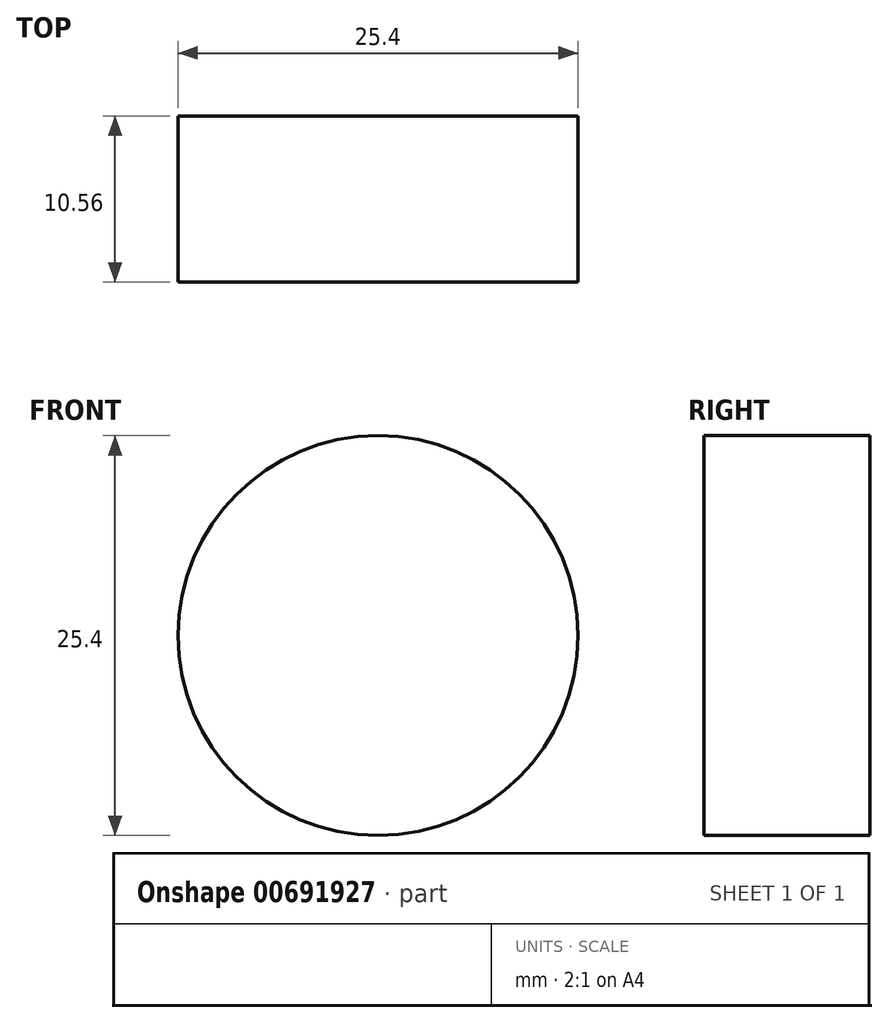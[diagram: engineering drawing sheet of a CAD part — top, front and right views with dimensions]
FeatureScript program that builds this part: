
annotation { "Feature Type Name" : "Feature", "Feature Type Description" : "" }
export const myFeature = defineFeature(function(context is Context, id is Id, definition is map)
    precondition{}
    {
        {
            var Q0;
            Q0=qCreatedBy(makeId("Front.planeOp"),FACE);
            var sketch = newSketch(context, id + "F0", { "sketchPlane" : qUnion([Q0])});
            skCircle(sketch, "E0", {"center": v(39.91, 0) * mm, "radius": 12.7 * mm});
            skSolve(sketch);
        }
        {
            var Q0;
            Q0=makeQuery(id+"F0.imprint","IMPRINT",FACE,{"disambiguationData":[TD([[makeQuery(id+"F0.imprint","IMPRINT",EDGE,{"derivedFrom":sQuery(id+"F0.wireOp",EDGE,"E0")}),1.0]])]});
            extrude(context, id + "F1", {"entities" : qUnion([Q0]), "oppositeDirection" : true, "depth" : 10.56 * mm, "offsetDistance" : 25.4 * mm});
        }
    });
